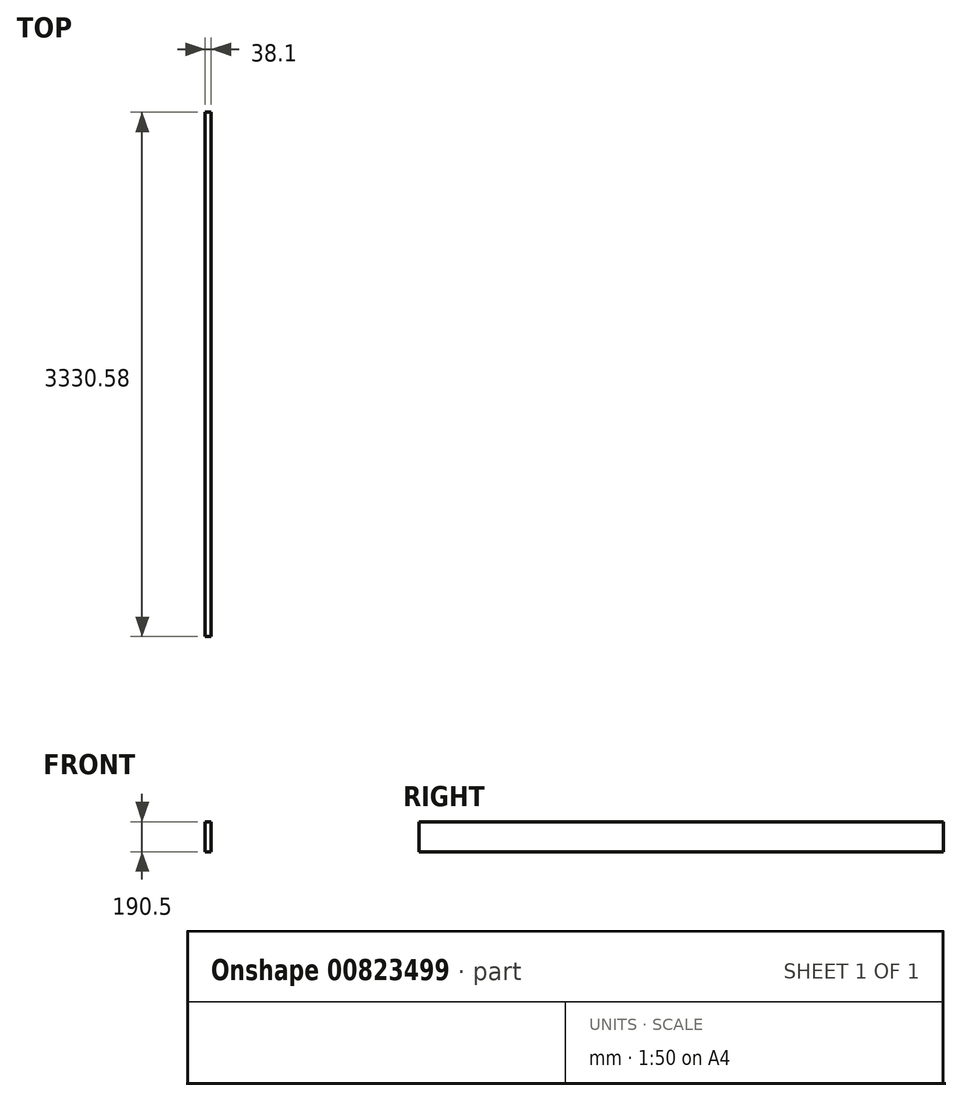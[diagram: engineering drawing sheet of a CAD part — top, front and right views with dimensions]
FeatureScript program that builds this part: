
annotation { "Feature Type Name" : "Feature", "Feature Type Description" : "" }
export const myFeature = defineFeature(function(context is Context, id is Id, definition is map)
    precondition{}
    {
        {
            var Q0;
            Q0=qCreatedBy(makeId("Front.planeOp"),FACE);
            var sketch = newSketch(context, id + "F0", { "sketchPlane" : qUnion([Q0])});
            skLineSegment(sketch, "E0.bottom", {"start": v(0, 0) * mm, "end": v(38.1, 0) * mm});
            skLineSegment(sketch, "E0.top", {"start": v(0, 190.5) * mm, "end": v(38.1, 190.5) * mm});
            skLineSegment(sketch, "E0.left", {"start": v(0, 0) * mm, "end": v(0, 190.5) * mm});
            skLineSegment(sketch, "E0.right", {"start": v(38.1, 0) * mm, "end": v(38.1, 190.5) * mm});
            skSolve(sketch);
        }
        {
            var Q0;
            Q0=qSketchRegion(id+"F0",true);
            extrude(context, id + "F1", {"entities" : qUnion([Q0]), "depth" : 3330.57 * mm, "offsetDistance" : 25.4 * mm});
        }
    });
